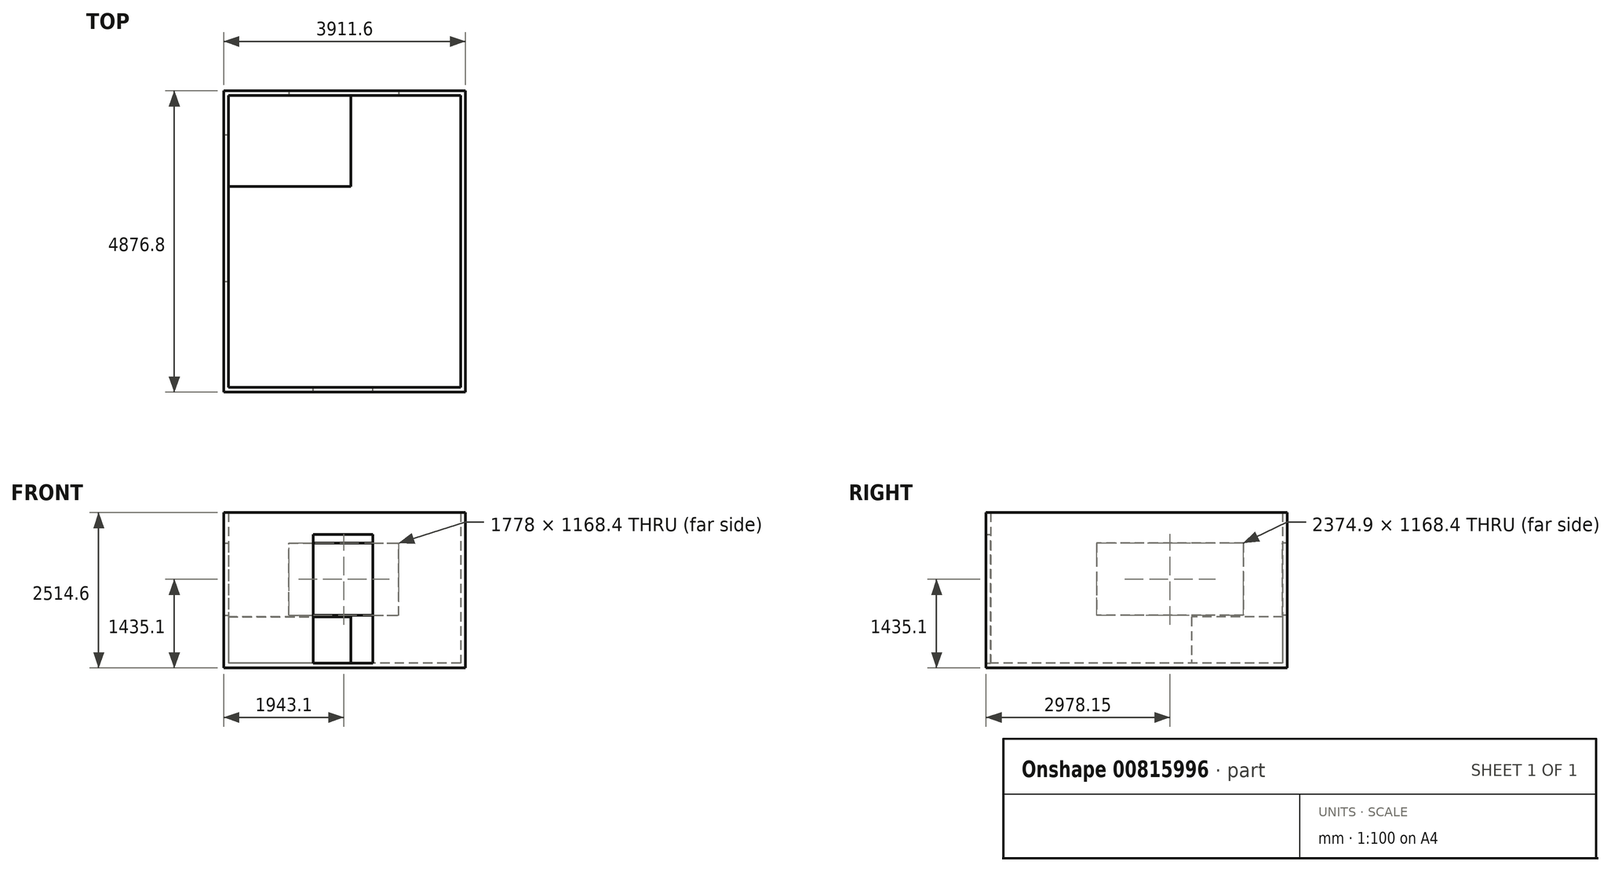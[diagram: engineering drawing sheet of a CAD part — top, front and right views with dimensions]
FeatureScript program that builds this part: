
annotation { "Feature Type Name" : "Feature", "Feature Type Description" : "" }
export const myFeature = defineFeature(function(context is Context, id is Id, definition is map)
    precondition{}
    {
        {
            var Q0;
            Q0=qCreatedBy(makeId("Top.planeOp"),FACE);
            var sketch = newSketch(context, id + "F0", { "sketchPlane" : qUnion([Q0])});
            skLineSegment(sketch, "E0.bottom", {"start": v(1879.6, 2362.2) * mm, "end": v(-1879.6, 2362.2) * mm});
            skLineSegment(sketch, "E0.top", {"start": v(1879.6, -2362.2) * mm, "end": v(-1879.6, -2362.2) * mm});
            skLineSegment(sketch, "E0.left", {"start": v(1879.6, 2362.2) * mm, "end": v(1879.6, -2362.2) * mm});
            skLineSegment(sketch, "E0.right", {"start": v(-1879.6, 2362.2) * mm, "end": v(-1879.6, -2362.2) * mm});
            skPoint(sketch, "E0.middle", {"position": v(0, 0) * mm});
            skSolve(sketch);
        }
        {
            var Q0;
            Q0 = qSketchRegion(id + "F0", true);
            extrude(context, id + "F1", {"entities" : qUnion([Q0]), "depth" : 2438.4 * mm, "offsetDistance" : 25.4 * mm});
        }
        {
            var Q0;
            Q0=makeQuery(id+"F1.opExtrude","CAP_FACE",FACE,{"disambiguationData":[OSD([sQuery(id+"F0.wireOp",EDGE,"E0.bottom"),sQuery(id+"F0.wireOp",EDGE,"E0.top"),sQuery(id+"F0.wireOp",EDGE,"E0.left"),sQuery(id+"F0.wireOp",EDGE,"E0.right")])],"isStart":false});
            shell(context, id + "F2", {"entities" : qUnion([Q0]), "thickness" : 76.2 * mm, "oppositeDirection" : true});
        }
        {
            var Q0;
            Q0=makeQuery(id+"F2.opShell","OFFSET_FACE",FACE,{"disambiguationData":[OSD([sQuery(id+"F0.wireOp",EDGE,"E0.top")])]});
            var sketch = newSketch(context, id + "F3", { "sketchPlane" : qUnion([Q0])});
            skLineSegment(sketch, "E1.bottom", {"start": v(-457.2, 0) * mm, "end": v(508, 0) * mm});
            skLineSegment(sketch, "E1.top", {"start": v(-457.2, 2082.8) * mm, "end": v(508, 2082.8) * mm});
            skLineSegment(sketch, "E1.left", {"start": v(-457.2, 0) * mm, "end": v(-457.2, 2082.8) * mm});
            skLineSegment(sketch, "E1.right", {"start": v(508, 0) * mm, "end": v(508, 2082.8) * mm});
            skSolve(sketch);
        }
        {
            var Q0;
            Q0 = qSketchRegion(id + "F3", true);
            extrude(context, id + "F4", {"entities" : qUnion([Q0]), "operationType" : NewBodyOperationType.REMOVE, "endBound" : BoundingType.THROUGH_ALL, "oppositeDirection" : true, "depth" : 3895.83 * mm, "offsetDistance" : 25.4 * mm});
        }
        {
            var Q0;
            Q0=makeQuery(id+"F2.opShell","OFFSET_FACE",FACE,{"disambiguationData":[OSD([sQuery(id+"F0.wireOp",EDGE,"E0.right")])]});
            var sketch = newSketch(context, id + "F5", { "sketchPlane" : qUnion([Q0])});
            skLineSegment(sketch, "E2.bottom", {"start": v(1727.2, 1943.1) * mm, "end": v(-647.7, 1943.1) * mm});
            skLineSegment(sketch, "E2.top", {"start": v(1727.2, 774.7) * mm, "end": v(-647.7, 774.7) * mm});
            skLineSegment(sketch, "E2.left", {"start": v(1727.2, 1943.1) * mm, "end": v(1727.2, 774.7) * mm});
            skLineSegment(sketch, "E2.right", {"start": v(-647.7, 1943.1) * mm, "end": v(-647.7, 774.7) * mm});
            skSolve(sketch);
        }
        {
            var Q0;
            Q0 = qSketchRegion(id + "F5", true);
            extrude(context, id + "F6", {"entities" : qUnion([Q0]), "operationType" : NewBodyOperationType.REMOVE, "endBound" : BoundingType.THROUGH_ALL, "oppositeDirection" : true, "depth" : 25.4 * mm, "offsetDistance" : 25.4 * mm});
        }
        {
            var Q0;
            Q0=makeQuery(id+"F2.opShell","OFFSET_FACE",FACE,{"disambiguationData":[OSD([sQuery(id+"F0.wireOp",EDGE,"E0.bottom")])]});
            var sketch = newSketch(context, id + "F7", { "sketchPlane" : qUnion([Q0])});
            skLineSegment(sketch, "E3.bottom", {"start": v(-901.7, 774.7) * mm, "end": v(876.3, 774.7) * mm});
            skLineSegment(sketch, "E3.top", {"start": v(-901.7, 1943.1) * mm, "end": v(876.3, 1943.1) * mm});
            skLineSegment(sketch, "E3.left", {"start": v(-901.7, 774.7) * mm, "end": v(-901.7, 1943.1) * mm});
            skLineSegment(sketch, "E3.right", {"start": v(876.3, 774.7) * mm, "end": v(876.3, 1943.1) * mm});
            skSolve(sketch);
        }
        {
            var Q0;
            Q0 = qSketchRegion(id + "F7", true);
            extrude(context, id + "F8", {"entities" : qUnion([Q0]), "operationType" : NewBodyOperationType.REMOVE, "endBound" : BoundingType.THROUGH_ALL, "oppositeDirection" : true, "depth" : 25.4 * mm, "offsetDistance" : 25.4 * mm});
        }
        {
            var Q0;
            Q0=makeQuery(id+"F4.boolean.opBoolean","MERGE",FACE,{"derivedFrom":[makeQuery(id+"F2.opShell","OFFSET_FACE",FACE,{"disambiguationData":[OSD([sQuery(id+"F0.wireOp",EDGE,"E0.bottom"),sQuery(id+"F0.wireOp",EDGE,"E0.top"),sQuery(id+"F0.wireOp",EDGE,"E0.left"),sQuery(id+"F0.wireOp",EDGE,"E0.right")])]}),makeQuery(id+"F4.opExtrude","SWEPT_FACE",FACE,{"disambiguationData":[OSD([sQuery(id+"F3.wireOp",EDGE,"E1.bottom")])]})]});
            var sketch = newSketch(context, id + "F9", { "sketchPlane" : qUnion([Q0])});
            skLineSegment(sketch, "E4.bottom", {"start": v(-1879.6, 2362.2) * mm, "end": v(101.6, 2362.2) * mm});
            skLineSegment(sketch, "E4.top", {"start": v(-1879.6, 889) * mm, "end": v(101.6, 889) * mm});
            skLineSegment(sketch, "E4.left", {"start": v(-1879.6, 2362.2) * mm, "end": v(-1879.6, 889) * mm});
            skLineSegment(sketch, "E4.right", {"start": v(101.6, 2362.2) * mm, "end": v(101.6, 889) * mm});
            skSolve(sketch);
        }
        {
            var Q0;
            Q0 = qSketchRegion(id + "F9", true);
            extrude(context, id + "F10", {"entities" : qUnion([Q0]), "depth" : 749.3 * mm, "offsetDistance" : 25.4 * mm});
        }
    });
